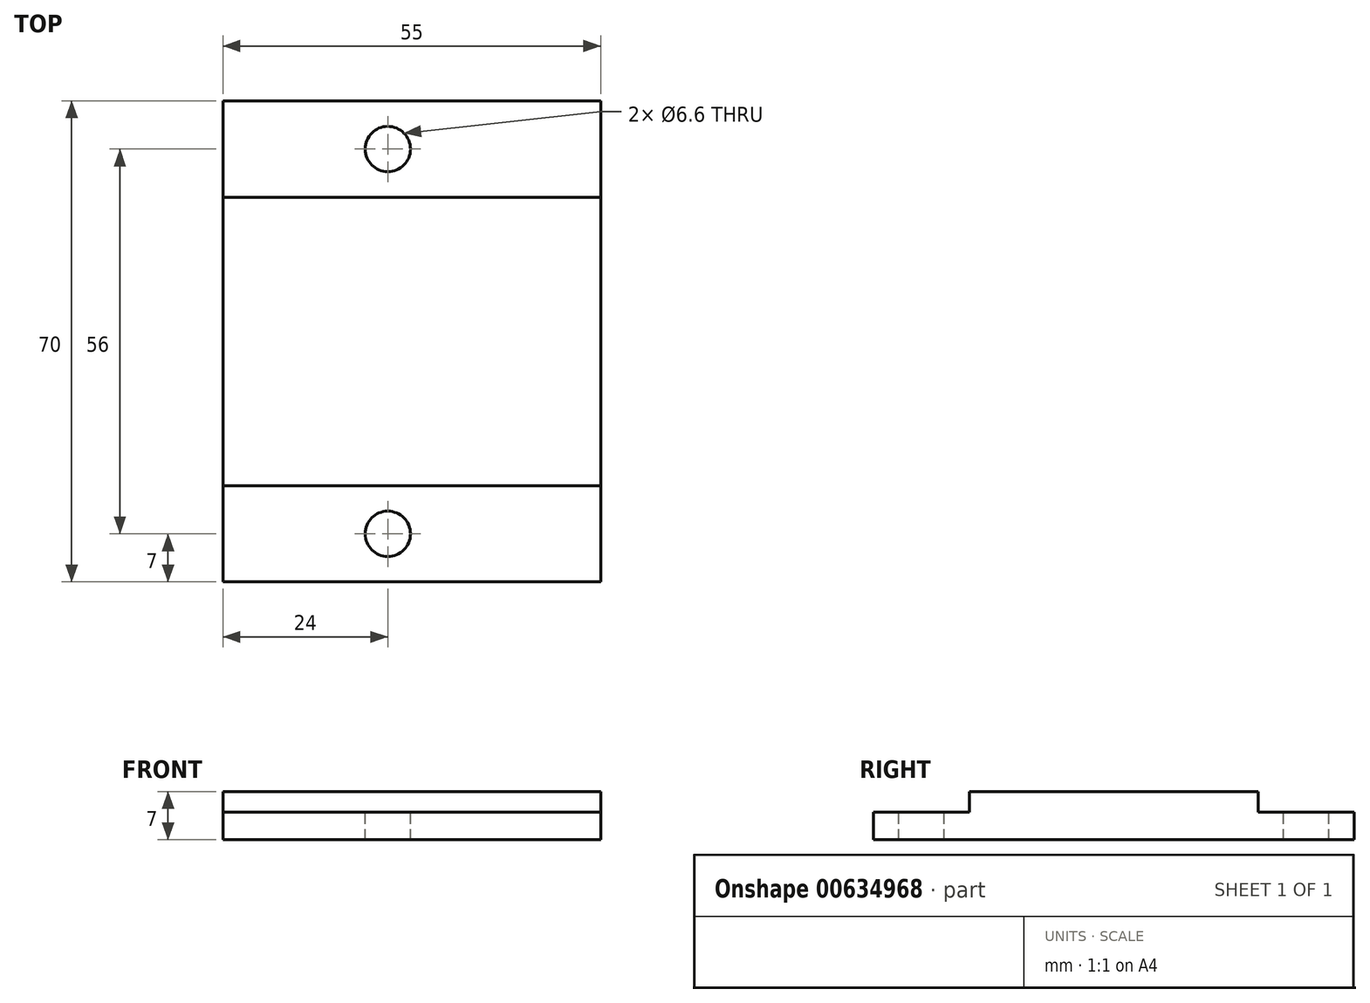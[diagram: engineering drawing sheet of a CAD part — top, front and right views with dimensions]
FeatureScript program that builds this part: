
annotation { "Feature Type Name" : "Feature", "Feature Type Description" : "" }
export const myFeature = defineFeature(function(context is Context, id is Id, definition is map)
    precondition{}
    {
        {
            var Q0;
            Q0=qCreatedBy(makeId("Top.planeOp"),FACE);
            var sketch = newSketch(context, id + "F0", { "sketchPlane" : qUnion([Q0])});
            skLineSegment(sketch, "E0.0", {"start": v(0, -35) * mm, "end": v(-55.17, -35) * mm});
            skLineSegment(sketch, "E0.1.0", {"start": v(0, -21) * mm, "end": v(0, -35) * mm});
            skLineSegment(sketch, "E0.1.1", {"start": v(0, -35) * mm, "end": v(-55, -35) * mm});
            skLineSegment(sketch, "E0.1.2", {"start": v(-55, -35) * mm, "end": v(-55, -21) * mm});
            skLineSegment(sketch, "E0.1.3", {"start": v(-55, -21) * mm, "end": v(0, -21) * mm});
            skLineSegment(sketch, "E1.0.0", {"start": v(-55, 35) * mm, "end": v(0, 35) * mm});
            skLineSegment(sketch, "E1.0.1", {"start": v(0, 35) * mm, "end": v(0, 21) * mm});
            skLineSegment(sketch, "E1.0.2", {"start": v(0, 21) * mm, "end": v(-55, 21) * mm});
            skLineSegment(sketch, "E1.0.3", {"start": v(-55, 21) * mm, "end": v(-55, 35) * mm});
            skCircle(sketch, "E2.0", {"center": v(-31, -28) * mm, "radius": 3.3 * mm});
            skLineSegment(sketch, "E3", {"start": v(-55, -21) * mm, "end": v(-55, 21) * mm});
            skLineSegment(sketch, "E4", {"start": v(0, -21) * mm, "end": v(0, 21) * mm});
            skCircle(sketch, "E5.MirrorC", {"center": v(-31, 28) * mm, "radius": 3.3 * mm});
            skSolve(sketch);
        }
        {
            var Q0;
            Q0=makeQuery(id+"F0.imprint","IMPRINT",FACE,{"disambiguationData":[TD([[makeQuery(id+"F0.imprint","IMPRINT",EDGE,{"derivedFrom":sQuery(id+"F0.wireOp",EDGE,"E1.0.0")}),-1.0]])]});
            var Q1;
            Q1=makeQuery(id+"F0.imprint","IMPRINT",FACE,{"disambiguationData":[TD([[makeQuery(id+"F0.imprint","IMPRINT",EDGE,{"derivedFrom":sQuery(id+"F0.wireOp",EDGE,"E0.1.3")}),1.0]])]});
            var Q2;
            Q2=makeQuery(id+"F0.imprint","IMPRINT",FACE,{"disambiguationData":[TD([[makeQuery(id+"F0.imprint","IMPRINT",EDGE,{"derivedFrom":sQuery(id+"F0.wireOp",EDGE,"E0.1.0")}),-1.0]])]});
            extrude(context, id + "F1", {"entities" : qUnion([Q0, Q1, Q2]), "oppositeDirection" : true, "depth" : 4 * mm, "offsetDistance" : 25 * mm});
        }
        {
            var Q0;
            Q0=makeQuery(id+"F0.imprint","IMPRINT",FACE,{"disambiguationData":[TD([[makeQuery(id+"F0.imprint","IMPRINT",EDGE,{"derivedFrom":sQuery(id+"F0.wireOp",EDGE,"E0.1.3")}),1.0]])]});
            extrude(context, id + "F2", {"entities" : qUnion([Q0]), "operationType" : NewBodyOperationType.ADD, "depth" : 3 * mm, "offsetDistance" : 25 * mm});
        }
    });
